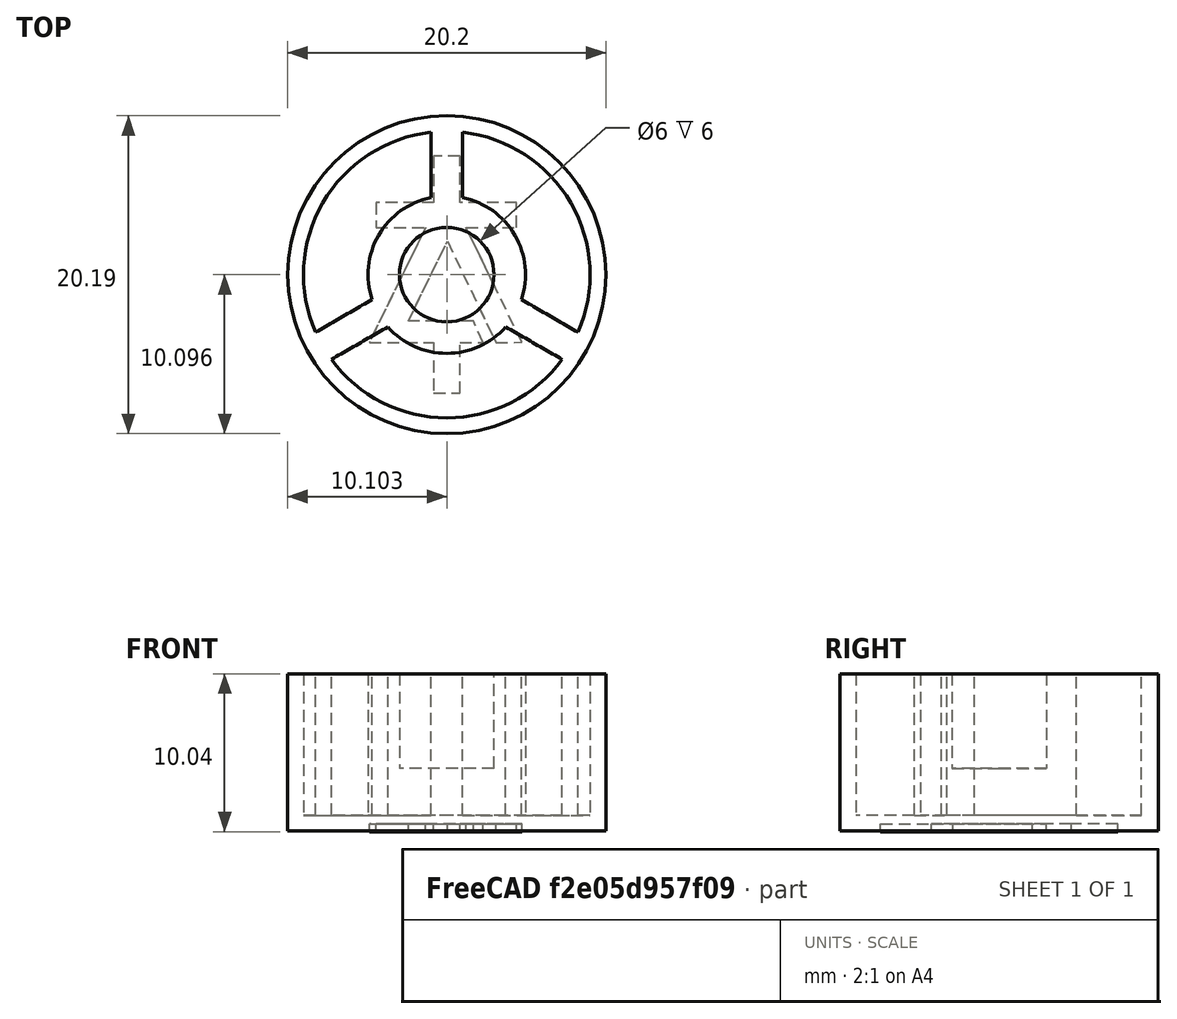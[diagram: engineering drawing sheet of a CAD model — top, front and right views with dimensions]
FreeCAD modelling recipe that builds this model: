
FCSTD DOCUMENT  (FreeCAD 0.14R3702 (Git))
Label: button
License: CC-BY 3.0
LicenseURL: http://creativecommons.org/licenses/by/3.0/
objects: Part::Feature×17, Part::Extrusion×9, Part::Cut×5, App::DocumentObjectGroup×3, Part::RuledSurface×3, Part::MultiFuse×2, Part::Mirroring×2
note: 38 computed .brp shape members not serialized (recipe doc carries the construction recipe); baked Part::Feature solids carry a one-line shape summary decoded from their .brp

FEATURE [App::DocumentObjectGroup] _  label="0"
FEATURE [Part::Feature] Line023 .. Line026  x4 (patterned run collapsed; names and placements below)
  shape: bbox 3.589 x 2.072 x 2e-07 mm, 0 faces, 0 solids (baked)
FEATURE [Part::Feature] Line027
  shape: bbox 2e-07 x 4.144 x 2e-07 mm, 0 faces, 0 solids (baked)
FEATURE [Part::Feature] Line028
  shape: bbox 2e-07 x 4.144 x 2e-07 mm, 0 faces, 0 solids (baked)
FEATURE [Part::Feature] Arc
  shape: bbox 14.66 x 3.711 x 2e-07 mm, 0 faces, 0 solids (baked)
FEATURE [Part::Feature] Arc001
  shape: bbox 4 x 6.482 x 2e-07 mm, 0 faces, 0 solids (baked)
FEATURE [Part::Feature] Arc002
  shape: bbox 8.098 x 12.7 x 2e-07 mm, 0 faces, 0 solids (baked)
FEATURE [Part::Feature] Arc003
  shape: bbox 8.098 x 12.7 x 2e-07 mm, 0 faces, 0 solids (baked)
FEATURE [Part::Feature] Arc004
  shape: bbox 4 x 6.482 x 2e-07 mm, 0 faces, 0 solids (baked)
FEATURE [Part::Feature] Arc005
  shape: bbox 7.485 x 1.684 x 2e-07 mm, 0 faces, 0 solids (baked)
FEATURE [App::DocumentObjectGroup] interne
  Group = -> [Line023,Line024,Line025,Line026,Line027,Line028,Arc,Arc001,Arc002,Arc003,Arc004,Arc005]
FEATURE [App::DocumentObjectGroup] button
  Group = -> [_,interne]
FEATURE [Part::RuledSurface] Ruled_Surface
  Curve1 = -> Arc004
  Curve2 = -> Arc003
  Orientation = 0
FEATURE [Part::RuledSurface] Ruled_Surface001
  Curve1 = -> Arc002
  Curve2 = -> Arc001
  Orientation = 0
FEATURE [Part::RuledSurface] Ruled_Surface002
  Curve1 = -> Arc005
  Curve2 = -> Arc
  Orientation = 0
FEATURE [Part::Extrusion] Extrude
  Base = -> Ruled_Surface
  Dir = (0,0,10)
  Solid = false
FEATURE [Part::Extrusion] Extrude035
  Base = -> Ruled_Surface001
  Dir = (0,0,10)
  Solid = false
FEATURE [Part::Extrusion] Extrude036
  Base = -> Ruled_Surface002
  Dir = (0,0,10)
  Solid = false
FEATURE [Part::Feature] Face
  Placement = pos=(0,0,0) rot=(-0.307964,0.931435,0.193874;1.71858rad)
  shape: bbox 10.55 x 17.35 x 20.09 mm, 1 faces, 0 solids (baked)
FEATURE [Part::Feature] Face001
  shape: bbox 6 x 6 x 2e-07 mm, 1 faces, 0 solids (baked)
FEATURE [Part::Extrusion] Extrude037  label="avant"
  Base = -> Face
  Dir = (0,0,1)
  Solid = false
FEATURE [Part::Feature] Face002
  Placement = pos=(0,0,1) rot=(0,0,1;0rad)
  shape: bbox 20.2 x 20.2 x 2e-07 mm, 1 faces, 0 solids (baked)
FEATURE [Part::Extrusion] Extrude038  label="corps"
  Base = -> Face002
  Dir = (0,0,9)
  Solid = false
FEATURE [Part::Cut] Cut
  Base = -> Extrude038
  Tool = -> Extrude036
FEATURE [Part::Cut] Cut001
  Base = -> Cut
  Tool = -> Extrude035
FEATURE [Part::Cut] Cut002
  Base = -> Cut001
  Tool = -> Extrude
FEATURE [Part::Feature] Face003
  Placement = pos=(0,0,4) rot=(0,0,1;0rad)
  shape: bbox 6 x 6 x 2e-07 mm, 1 faces, 0 solids (baked)
FEATURE [Part::Extrusion] Extrude039
  Base = -> Face001
  Dir = (0,0,4)
  Solid = false
FEATURE [Part::Extrusion] Extrude040
  Base = -> Face003
  Dir = (0,0,6)
  Solid = false
FEATURE [Part::Cut] Cut003
  Base = -> Cut002
  Tool = -> Extrude040
FEATURE [Part::MultiFuse] Fusion
  Shapes = -> [Extrude037,Extrude039]
FEATURE [Part::MultiFuse] Fusion001
  Shapes = -> [Fusion,Cut003]
FEATURE [Part::Feature] Face004
  shape: bbox 9.684 x 15.06 x 2e-07 mm, 1 faces, 0 solids (baked)
FEATURE [Part::Extrusion] Extrude041  label="logo"
  Base = -> Face004
  Dir = (0,0,0.5)
  Solid = false
FEATURE [Part::Mirroring] Part__Mirroring  label="logo (Mirror #1)"
  Base = (0,0,0)
  Normal = (1,0,0)
  Placement = pos=(1.90489,2.00952e-05,-0.0368169) rot=(0,0,1;0rad)
  Source = -> Extrude041
FEATURE [Part::Cut] Cut004  label="bouton"
  Base = -> Fusion001
  Tool = -> Part__Mirroring
FEATURE [Part::Extrusion] Extrude042  label="logo001"
  Base = -> Face004
  Dir = (0,0,0.5)
  Solid = false
FEATURE [Part::Mirroring] Part__Mirroring001  label="logo (Mirror #1)001"
  Base = (0,0,0)
  Normal = (1,0,0)
  Placement = pos=(1.90489,2.00952e-05,-0.0368169) rot=(0,0,1;0rad)
  Source = -> Extrude042
